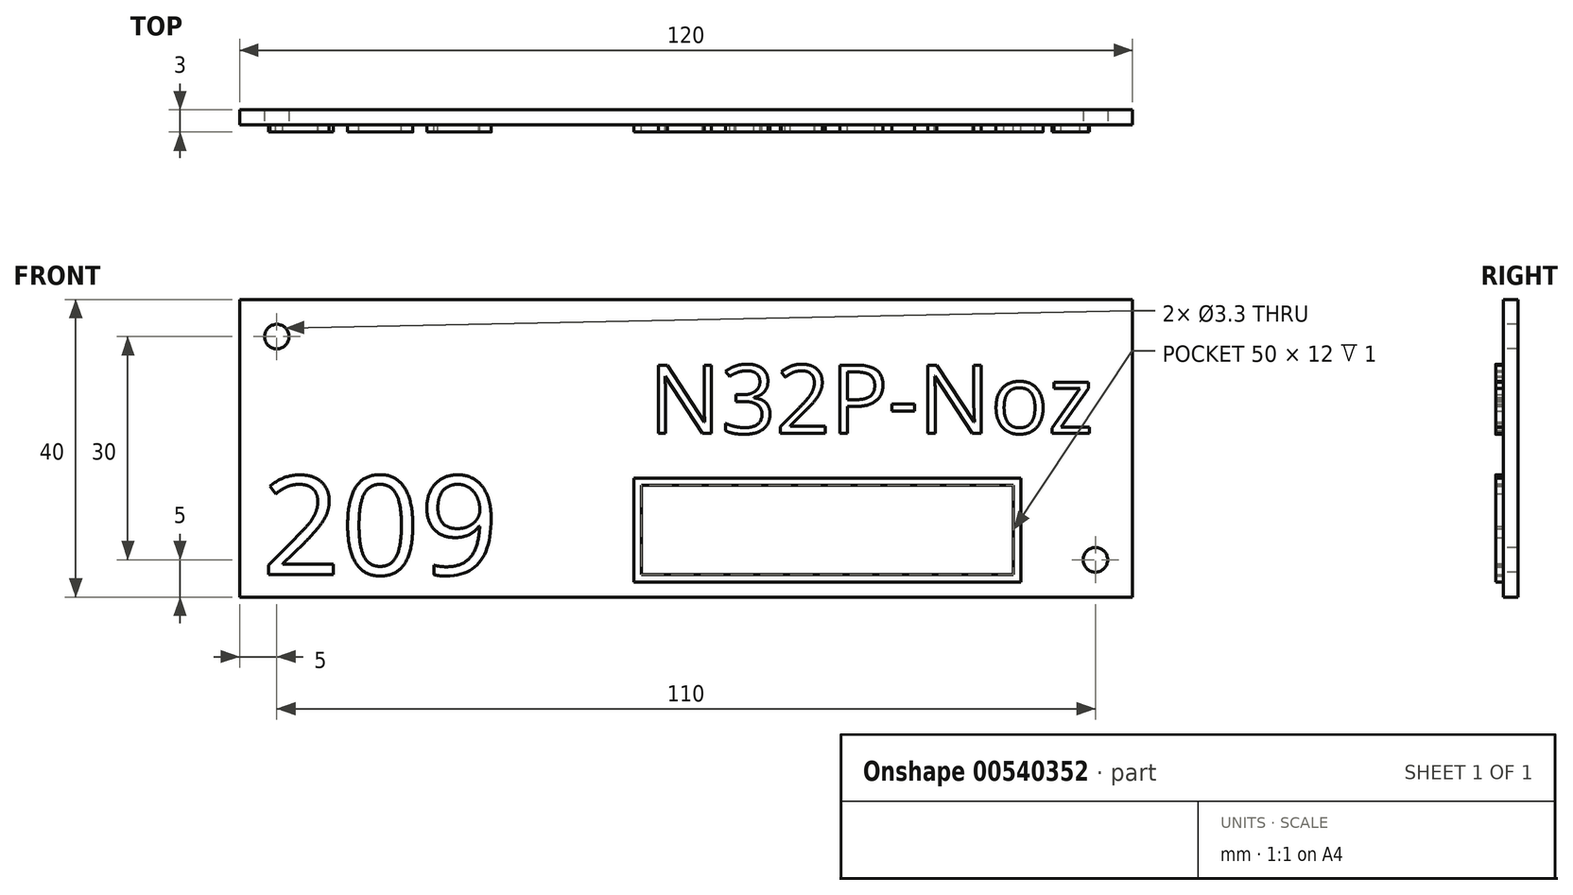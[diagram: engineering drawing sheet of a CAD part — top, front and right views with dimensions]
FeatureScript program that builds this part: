
annotation { "Feature Type Name" : "Feature", "Feature Type Description" : "" }
export const myFeature = defineFeature(function(context is Context, id is Id, definition is map)
    precondition{}
    {
        {
            var Q0;
            Q0=qCreatedBy(makeId("Front.planeOp"),FACE);
            var sketch = newSketch(context, id + "F0", { "sketchPlane" : qUnion([Q0])});
            skLineSegment(sketch, "E0.bottom", {"start": v(60, -20) * mm, "end": v(-60, -20) * mm});
            skLineSegment(sketch, "E0.top", {"start": v(60, 20) * mm, "end": v(-60, 20) * mm});
            skLineSegment(sketch, "E0.left", {"start": v(60, -20) * mm, "end": v(60, 20) * mm});
            skLineSegment(sketch, "E0.right", {"start": v(-60, -20) * mm, "end": v(-60, 20) * mm});
            skPoint(sketch, "E0.middle", {"position": v(0, 0) * mm});
            skSolve(sketch);
        }
        {
            var Q0;
            Q0=makeQuery(id+"F0.imprint","IMPRINT",FACE,{"disambiguationData":[TD([[makeQuery(id+"F0.imprint","IMPRINT",EDGE,{"derivedFrom":sQuery(id+"F0.wireOp",EDGE,"E0.bottom")}),-1.0]])]});
            extrude(context, id + "F1", {"entities" : qUnion([Q0]), "depth" : 2 * mm});
        }
        {
            var Q0;
            Q0=makeQuery(id+"F1.opExtrude","CAP_FACE",FACE,{"disambiguationData":[OSD([sQuery(id+"F0.wireOp",EDGE,"E0.bottom"),sQuery(id+"F0.wireOp",EDGE,"E0.top"),sQuery(id+"F0.wireOp",EDGE,"E0.left"),sQuery(id+"F0.wireOp",EDGE,"E0.right")])],"isStart":false});
            var sketch = newSketch(context, id + "F2", { "sketchPlane" : qUnion([Q0])});
            skPoint(sketch, "E1", {"position": v(-55, 15) * mm});
            skPoint(sketch, "E2", {"position": v(55, -15) * mm});
            skSolve(sketch);
        }
        {
            var Q0;
            Q0=sQuery(id+"F2.wireOp",VERTEX,"E1");
            var Q1;
            Q1=sQuery(id+"F2.wireOp",VERTEX,"E2");
            var Q2;
            Q2=makeQuery(id+"F1.opExtrude","SWEPT_BODY",BODY,{"disambiguationData":[OSD([sQuery(id+"F0.wireOp",EDGE,"E0.bottom"),sQuery(id+"F0.wireOp",EDGE,"E0.top"),sQuery(id+"F0.wireOp",EDGE,"E0.left"),sQuery(id+"F0.wireOp",EDGE,"E0.right")])]});
            hole(context, id + "F3", {"style" : HoleStyle.SIMPLE, "endStyle" : HoleEndStyle.THROUGH, "holeDiameter" : 3.3 * mm, "locations" : qUnion([Q0, Q1]), "scope" : qUnion([Q2]), "isTappedThrough" : true});
        }
        {
            var Q0;
            Q0=makeQuery(id+"F1.opExtrude","CAP_FACE",FACE,{"disambiguationData":[OSD([sQuery(id+"F0.wireOp",EDGE,"E0.bottom"),sQuery(id+"F0.wireOp",EDGE,"E0.top"),sQuery(id+"F0.wireOp",EDGE,"E0.left"),sQuery(id+"F0.wireOp",EDGE,"E0.right")])],"isStart":false});
            var sketch = newSketch(context, id + "F4", { "sketchPlane" : qUnion([Q0])});
            skText(sketch, "E3", { "text": "N32P-Noz", "fontName": "OpenSans-Regular.ttf"});
            const initialGuessF4  = {"E3": [-0.005, 0.002, 1, 0, 0.00925]};
            skSetInitialGuess(sketch, initialGuessF4);
            skSolve(sketch);
        }
        {
            var Q0;
            Q0=qSketchRegion(id+"F4",true);
            extrude(context, id + "F5", {"entities" : qUnion([Q0]), "operationType" : NewBodyOperationType.ADD, "depth" : 1 * mm});
        }
        {
            var Q0;
            {var subQ0=sQuery(id+"F0.wireOp",EDGE,"E0.top");var subQ1=sQuery(id+"F0.wireOp",EDGE,"E0.left");var subQ2=sQuery(id+"F0.wireOp",EDGE,"E0.right");var subQ3=sQuery(id+"F0.wireOp",EDGE,"E0.bottom");Q0=makeQuery(id+"F5.boolean.opBoolean","SPLIT",FACE,{"disambiguationData":[TD([makeQuery(id+"F1.opExtrude","SWEPT_FACE",FACE,{"disambiguationData":[OSD([subQ3])]})])],"derivedFrom":makeQuery(id+"F1.opExtrude","CAP_FACE",FACE,{"disambiguationData":[OSD([subQ3,subQ0,subQ1,subQ2])],"isStart":false})});}
            var sketch = newSketch(context, id + "F6", { "sketchPlane" : qUnion([Q0])});
            skText(sketch, "E4", { "text": "209", "fontName": "OpenSans-Regular.ttf"});
            const initialGuessF6  = {"E4": [-0.057, -0.017, 1, 0, 0.01335]};
            skSetInitialGuess(sketch, initialGuessF6);
            skSolve(sketch);
        }
        {
            var Q0;
            Q0=qSketchRegion(id+"F6",true);
            extrude(context, id + "F7", {"entities" : qUnion([Q0]), "operationType" : NewBodyOperationType.ADD, "depth" : 1 * mm});
        }
        {
            var Q0;
            {var subQ46=sQuery(id+"F0.wireOp",EDGE,"E0.top");var subQ48=sQuery(id+"F0.wireOp",EDGE,"E0.left");var subQ66=sQuery(id+"F0.wireOp",EDGE,"E0.right");var subQ76=sQuery(id+"F0.wireOp",EDGE,"E0.bottom");var subQ77=makeQuery(id+"F1.opExtrude","SWEPT_FACE",FACE,{"disambiguationData":[OSD([subQ76])]});Q0=makeQuery(id+"F7.boolean.opBoolean","SPLIT",FACE,{"disambiguationData":[TD([subQ77])],"derivedFrom":makeQuery(id+"F5.boolean.opBoolean","SPLIT",FACE,{"disambiguationData":[TD([subQ77])],"derivedFrom":makeQuery(id+"F1.opExtrude","CAP_FACE",FACE,{"disambiguationData":[OSD([subQ76,subQ46,subQ48,subQ66])],"isStart":false})})});}
            var sketch = newSketch(context, id + "F8", { "sketchPlane" : qUnion([Q0])});
            skLineSegment(sketch, "E5.bottom", {"start": v(45, -18) * mm, "end": v(-7, -18) * mm});
            skLineSegment(sketch, "E5.top", {"start": v(45, -4) * mm, "end": v(-7, -4) * mm});
            skLineSegment(sketch, "E5.left", {"start": v(45, -18) * mm, "end": v(45, -4) * mm});
            skLineSegment(sketch, "E5.right", {"start": v(-7, -18) * mm, "end": v(-7, -4) * mm});
            skPoint(sketch, "E5.middle", {"position": v(19, -11) * mm});
            skLineSegment(sketch, "E6.0", {"start": v(44, -5) * mm, "end": v(-6, -5) * mm});
            skLineSegment(sketch, "E6.1", {"start": v(44, -17) * mm, "end": v(44, -5) * mm});
            skLineSegment(sketch, "E6.2", {"start": v(44, -17) * mm, "end": v(-6, -17) * mm});
            skLineSegment(sketch, "E6.3", {"start": v(-6, -17) * mm, "end": v(-6, -5) * mm});
            skSolve(sketch);
        }
        {
            var Q0;
            Q0=makeQuery(id+"F8.imprint","IMPRINT",FACE,{"disambiguationData":[TD([[makeQuery(id+"F8.imprint","IMPRINT",EDGE,{"derivedFrom":sQuery(id+"F8.wireOp",EDGE,"E5.bottom")}),-1.0]])]});
            extrude(context, id + "F9", {"entities" : qUnion([Q0]), "operationType" : NewBodyOperationType.ADD, "depth" : 1 * mm});
        }
    });
